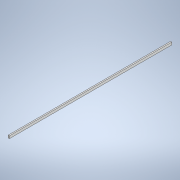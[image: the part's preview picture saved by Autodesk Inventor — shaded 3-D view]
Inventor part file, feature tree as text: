
AUTODESK INVENTOR PART (.ipt)
format: ipt  version: 2021 (Build 250183000, 183)  size: 97,792 bytes
history: native  units: in
note: dims shown in document units (in); Inventor stores cm internally (conversion verified against a paired STEP export)
features: extrude x1, sketch x1
ambient origin geometry x8: Origin, YZ Plane, XZ Plane, XY Plane, X Axis, Y Axis, Z Axis, Center Point
bodies: Solid1 (feature_tree)
feature tree (2):
  extrude  "Extrusion1"  Depth=0.523in
  sketch  "Sketch1"  dims[d0=66.9291in d1=0.523in d2=1.0in d3=0.0in]
